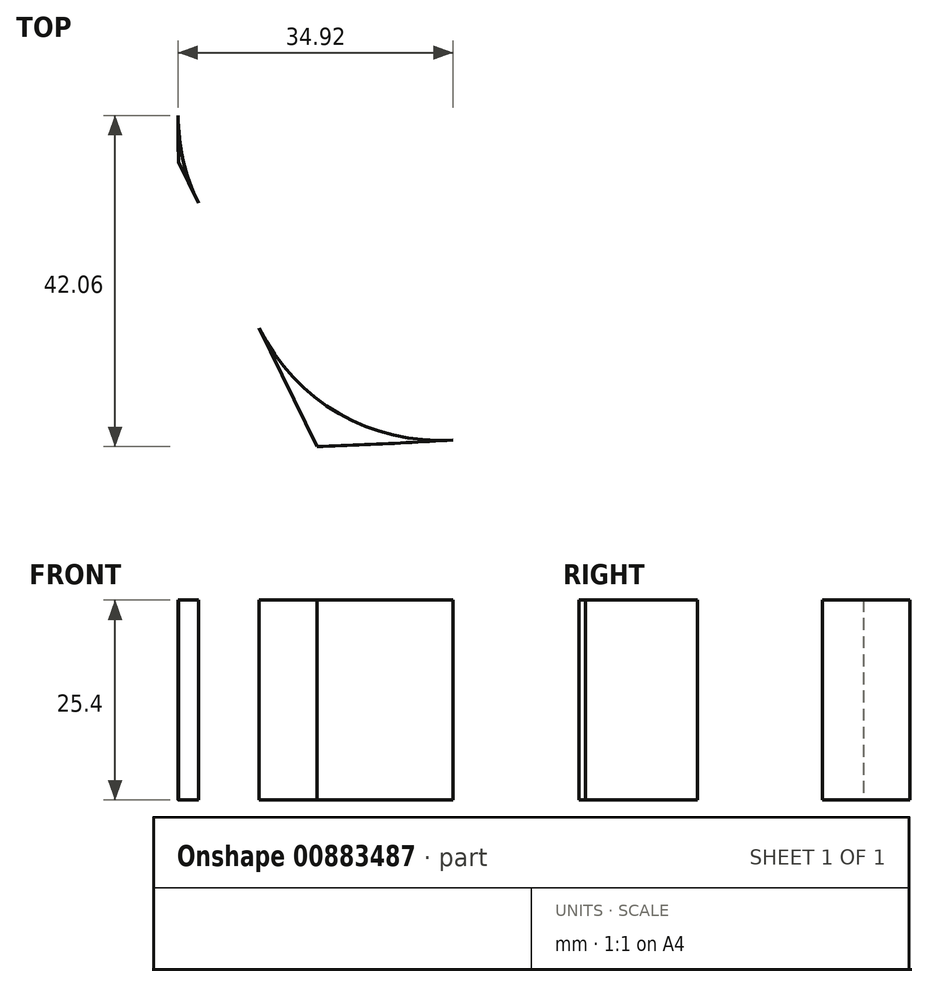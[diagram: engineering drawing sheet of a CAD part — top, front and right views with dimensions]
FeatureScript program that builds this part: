
annotation { "Feature Type Name" : "Feature", "Feature Type Description" : "" }
export const myFeature = defineFeature(function(context is Context, id is Id, definition is map)
    precondition{}
    {
        {
            var Q0;
            Q0=qCreatedBy(makeId("Top.planeOp"),FACE);
            var sketch = newSketch(context, id + "F0", { "sketchPlane" : qUnion([Q0])});
            skFitSpline(sketch, "E0", {"points": [v(-46.06, -16.49) * mm, v(-37.33, 27.67) * mm, v(5.57, 42.01) * mm, v(34.02, -31.54) * mm, v(-28.46, -52.62) * mm], "startDerivative": vector(-1.98, 213.89) * mm, "endDerivative": vector(-309.6, -12.08) * mm});
            skFitSpline(sketch, "E1", {"points": [v(-28.46, -52.62) * mm, v(-46.06, -16.49) * mm], "startDerivative": vector(-17.6, 36.13) * mm, "endDerivative": vector(-17.6, 36.13) * mm});
            skArc(sketch, "E2.filletArc", {"start": v(-35.8, -37.55) * mm, "mid": v(-25.67, -48.43) * mm, "end": v(-11.18, -51.77) * mm});
            skArc(sketch, "E3.filletArc", {"start": v(-46.1, -10.56) * mm, "mid": v(-45.45, -16.26) * mm, "end": v(-43.53, -21.68) * mm});
            skSolve(sketch);
        }
        {
            var Q0;
            Q0=makeQuery(id+"F0.imprint","IMPRINT",FACE,{"disambiguationData":[TD([[makeQuery(id+"F0.imprint","IMPRINT",EDGE,{"derivedFrom":sQuery(id+"F0.wireOp",EDGE,"E0")}),-1.0]])]});
            extrude(context, id + "F1", {"entities" : qUnion([Q0]), "depth" : 25.4 * mm, "offsetDistance" : 25.4 * mm});
        }
        {
            var Q0;
            Q0=makeQuery(id+"F1.opExtrude","CAP_FACE",FACE,{"disambiguationData":[OSD([sQuery(id+"F0.wireOp",EDGE,"E0"),sQuery(id+"F0.wireOp",EDGE,"E1"),sQuery(id+"F0.wireOp",EDGE,"E2.filletArc"),sQuery(id+"F0.wireOp",EDGE,"E3.filletArc")])],"isStart":false});
            var sketch = newSketch(context, id + "F2", { "sketchPlane" : qUnion([Q0])});
            skFitSpline(sketch, "E4", {"points": [v(-23.27, 0) * mm, v(0, 6.54) * mm, v(7.77, -11.3) * mm, v(-18.3, -16.67) * mm, v(-23.27, 0) * mm]});
            skSolve(sketch);
        }
        {
            var Q0;
            Q0 = qSketchRegion(id + "F2", true);
            extrude(context, id + "F3", {"entities" : qUnion([Q0]), "operationType" : NewBodyOperationType.REMOVE, "oppositeDirection" : true, "depth" : 104.9 * mm, "offsetDistance" : 25.4 * mm});
        }
    });
